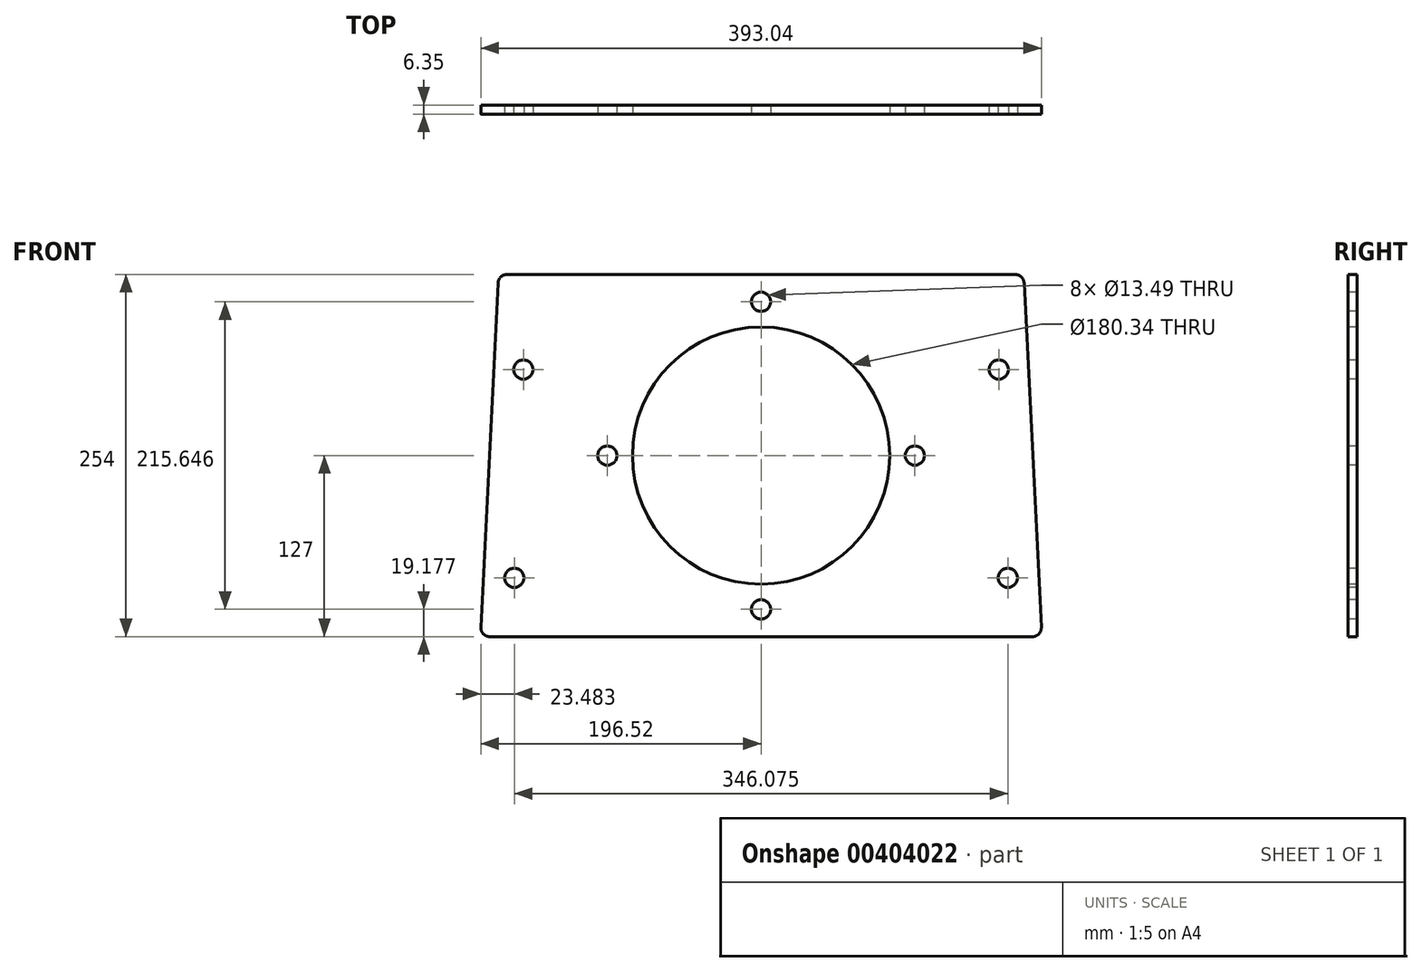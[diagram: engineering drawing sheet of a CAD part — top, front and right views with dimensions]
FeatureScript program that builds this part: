
annotation { "Feature Type Name" : "Feature", "Feature Type Description" : "" }
export const myFeature = defineFeature(function(context is Context, id is Id, definition is map)
    precondition{}
    {
        {
            var Q0;
            Q0=qCreatedBy(makeId("Front.planeOp"),FACE);
            var sketch = newSketch(context, id + "F0", { "sketchPlane" : qUnion([Q0])});
            skPoint(sketch, "E0.middle", {"position": v(0, 0) * mm});
            skLineSegment(sketch, "E1.top", {"start": v(-190.17, -127) * mm, "end": v(190.17, -127) * mm});
            skCircle(sketch, "E2", {"center": v(-166.69, 60.33) * mm, "radius": 6.75 * mm});
            skCircle(sketch, "E3.1.0.0", {"center": v(166.69, 60.32) * mm, "radius": 6.75 * mm});
            skCircle(sketch, "E4", {"center": v(173.04, -85.73) * mm, "radius": 6.75 * mm});
            skCircle(sketch, "E5", {"center": v(-173.04, -85.73) * mm, "radius": 6.75 * mm});
            skLineSegment(sketch, "E6", {"start": v(-178.1, 127) * mm, "end": v(178.1, 127) * mm});
            skLineSegment(sketch, "E7", {"start": v(-184.45, 120.97) * mm, "end": v(-196.52, -120.33) * mm});
            skLineSegment(sketch, "E8", {"start": v(184.45, 120.97) * mm, "end": v(196.52, -120.33) * mm});
            skPoint(sketch, "E9.visualSharp", {"position": v(-184.15, 127) * mm});
            skArc(sketch, "E9.filletArc", {"start": v(-178.1, 127) * mm, "mid": v(-182.49, 125.25) * mm, "end": v(-184.45, 120.97) * mm});
            skPoint(sketch, "E10.visualSharp", {"position": v(-196.85, -127) * mm});
            skArc(sketch, "E10.filletArc", {"start": v(-196.52, -120.33) * mm, "mid": v(-194.78, -125.03) * mm, "end": v(-190.17, -127) * mm});
            skPoint(sketch, "E11.visualSharp", {"position": v(196.85, -127) * mm});
            skArc(sketch, "E11.filletArc", {"start": v(190.17, -127) * mm, "mid": v(194.78, -125.03) * mm, "end": v(196.52, -120.33) * mm});
            skPoint(sketch, "E12.visualSharp", {"position": v(184.15, 127) * mm});
            skArc(sketch, "E12.filletArc", {"start": v(184.45, 120.97) * mm, "mid": v(182.49, 125.25) * mm, "end": v(178.1, 127) * mm});
            skPoint(sketch, "E13", {"position": v(0, -127) * mm});
            skSolve(sketch);
        }
        {
            var Q0;
            Q0 = qSketchRegion(id + "F0", true);
            extrude(context, id + "F1", {"entities" : qUnion([Q0]), "oppositeDirection" : true, "depth" : 6.35 * mm});
        }
        {
            var Q0;
            Q0=makeQuery(id+"F1.opExtrude","CAP_FACE",FACE,{"disambiguationData":[OSD([sQuery(id+"F0.wireOp",EDGE,"E1.bottom"),sQuery(id+"F0.wireOp",EDGE,"E1.top"),sQuery(id+"F0.wireOp",EDGE,"E1.left"),sQuery(id+"F0.wireOp",EDGE,"E1.right"),sQuery(id+"F0.wireOp",EDGE,"E2"),sQuery(id+"F0.wireOp",EDGE,"E3.0.1.0"),sQuery(id+"F0.wireOp",EDGE,"E3.1.0.0"),sQuery(id+"F0.wireOp",EDGE,"E3.1.1.0")])],"isStart":true});
            var sketch = newSketch(context, id + "F2", { "sketchPlane" : qUnion([Q0])});
            skCircle(sketch, "E14", {"center": v(0, 0) * mm, "radius": 90.17 * mm});
            skSolve(sketch);
        }
        {
            var Q0;
            Q0 = qSketchRegion(id + "F2", true);
            extrude(context, id + "F3", {"entities" : qUnion([Q0]), "operationType" : NewBodyOperationType.REMOVE, "endBound" : BoundingType.THROUGH_ALL, "oppositeDirection" : true, "depth" : 25.4 * mm});
        }
        {
            var Q0;
            Q0=makeQuery(id+"F1.opExtrude","CAP_FACE",FACE,{"disambiguationData":[OSD([sQuery(id+"F0.wireOp",EDGE,"E1.bottom"),sQuery(id+"F0.wireOp",EDGE,"E1.top"),sQuery(id+"F0.wireOp",EDGE,"E1.left"),sQuery(id+"F0.wireOp",EDGE,"E1.right"),sQuery(id+"F0.wireOp",EDGE,"E2"),sQuery(id+"F0.wireOp",EDGE,"E3.0.1.0"),sQuery(id+"F0.wireOp",EDGE,"E3.1.0.0"),sQuery(id+"F0.wireOp",EDGE,"E3.1.1.0")])],"isStart":true});
            var sketch = newSketch(context, id + "F4", { "sketchPlane" : qUnion([Q0])});
            skCircle(sketch, "E15", {"center": v(0, 107.82) * mm, "radius": 6.75 * mm});
            skCircle(sketch, "E16.1.0", {"center": v(-107.82, 0) * mm, "radius": 6.75 * mm});
            skCircle(sketch, "E16.2.0", {"center": v(0, -107.82) * mm, "radius": 6.75 * mm});
            skCircle(sketch, "E16.3.0", {"center": v(107.82, 0) * mm, "radius": 6.75 * mm});
            skPoint(sketch, "E16.center", {"position": v(0, 0) * mm});
            skSolve(sketch);
        }
        {
            var Q0;
            Q0 = qSketchRegion(id + "F4", true);
            extrude(context, id + "F5", {"entities" : qUnion([Q0]), "operationType" : NewBodyOperationType.REMOVE, "endBound" : BoundingType.THROUGH_ALL, "oppositeDirection" : true, "depth" : 25.4 * mm});
        }
        {
            var Q0;
            Q0=makeQuery(id+"F3.boolean.opBoolean","INTERSECT",EDGE,{"derivedFrom":[makeQuery(id+"F1.opExtrude","CAP_FACE",FACE,{"disambiguationData":[OSD([sQuery(id+"F0.wireOp",EDGE,"E1.bottom"),sQuery(id+"F0.wireOp",EDGE,"E1.top"),sQuery(id+"F0.wireOp",EDGE,"E1.left"),sQuery(id+"F0.wireOp",EDGE,"E1.right"),sQuery(id+"F0.wireOp",EDGE,"E2"),sQuery(id+"F0.wireOp",EDGE,"E3.0.1.0"),sQuery(id+"F0.wireOp",EDGE,"E3.1.0.0"),sQuery(id+"F0.wireOp",EDGE,"E3.1.1.0")])],"isStart":false}),makeQuery(id+"F3.opExtrude","SWEPT_FACE",FACE,{"disambiguationData":[OSD([sQuery(id+"F2.wireOp",EDGE,"E14")])]})]});
            var Q1;
            Q1=makeQuery(id+"F3.boolean.opBoolean","COPY",EDGE,{"derivedFrom":makeQuery(id+"F3.opExtrude","CAP_EDGE",EDGE,{"disambiguationData":[OSD([sQuery(id+"F2.wireOp",EDGE,"E14")])],"isStart":true})});
            fillet(context, id + "F6", {"entities" : qUnion([Q0, Q1]), "radius" : 0.5 * mm, "tangentPropagation" : true, "allowEdgeOverflow" : false});
        }
    });
